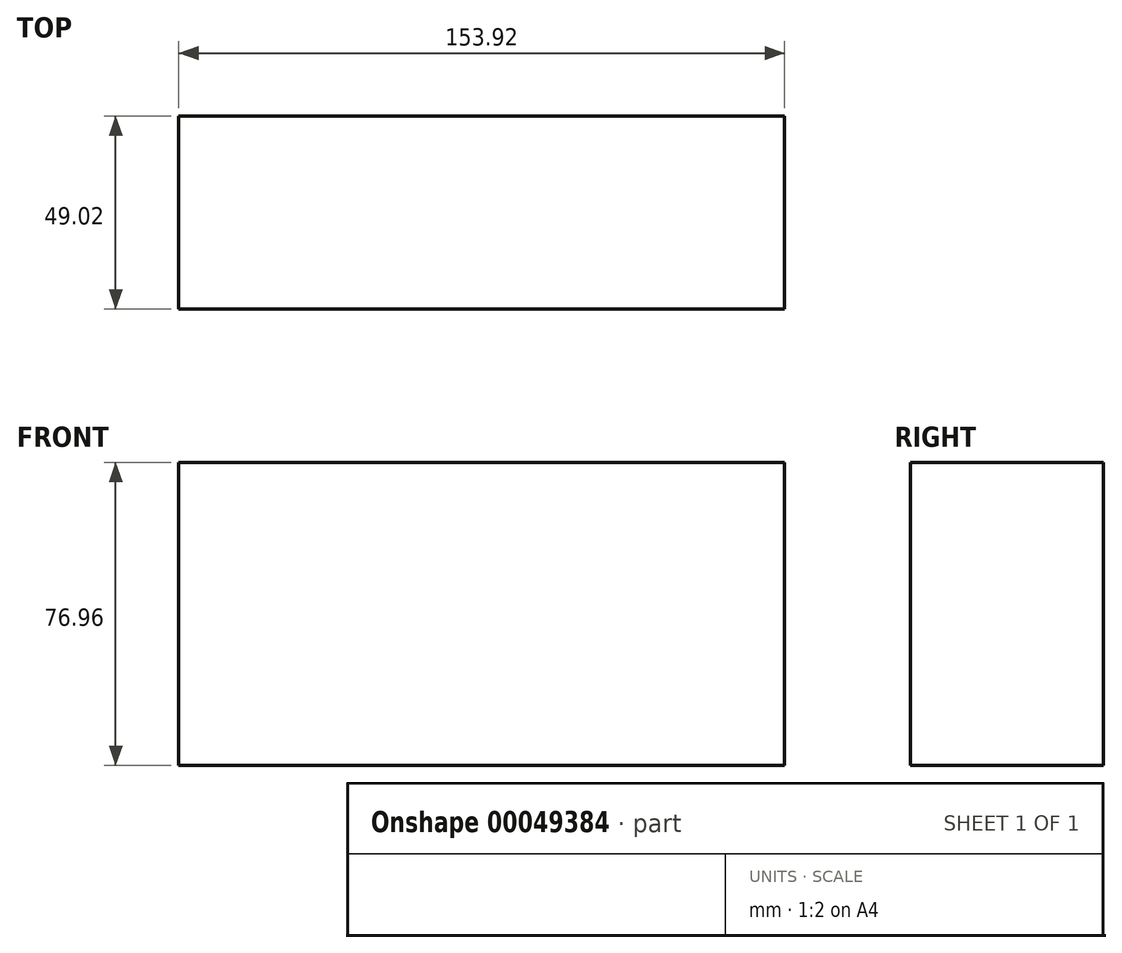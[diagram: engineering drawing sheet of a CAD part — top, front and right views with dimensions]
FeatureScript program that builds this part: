
annotation { "Feature Type Name" : "Feature", "Feature Type Description" : "" }
export const myFeature = defineFeature(function(context is Context, id is Id, definition is map)
    precondition{}
    {
        {
            var Q0;
            Q0=qCreatedBy(makeId("Top.planeOp"),FACE);
            var sketch = newSketch(context, id + "F0", { "sketchPlane" : qUnion([Q0])});
            skLineSegment(sketch, "E0.bottom", {"start": v(0, 0) * mm, "end": v(153.92, 0) * mm});
            skLineSegment(sketch, "E0.top", {"start": v(0, 49.02) * mm, "end": v(153.92, 49.02) * mm});
            skLineSegment(sketch, "E0.left", {"start": v(0, 0) * mm, "end": v(0, 49.02) * mm});
            skLineSegment(sketch, "E0.right", {"start": v(153.92, 0) * mm, "end": v(153.92, 49.02) * mm});
            skSolve(sketch);
        }
        {
            var Q0;
            Q0 = qSketchRegion(id + "F0", true);
            extrude(context, id + "F1", {"entities" : qUnion([Q0]), "depth" : 76.96 * mm});
        }
    });
